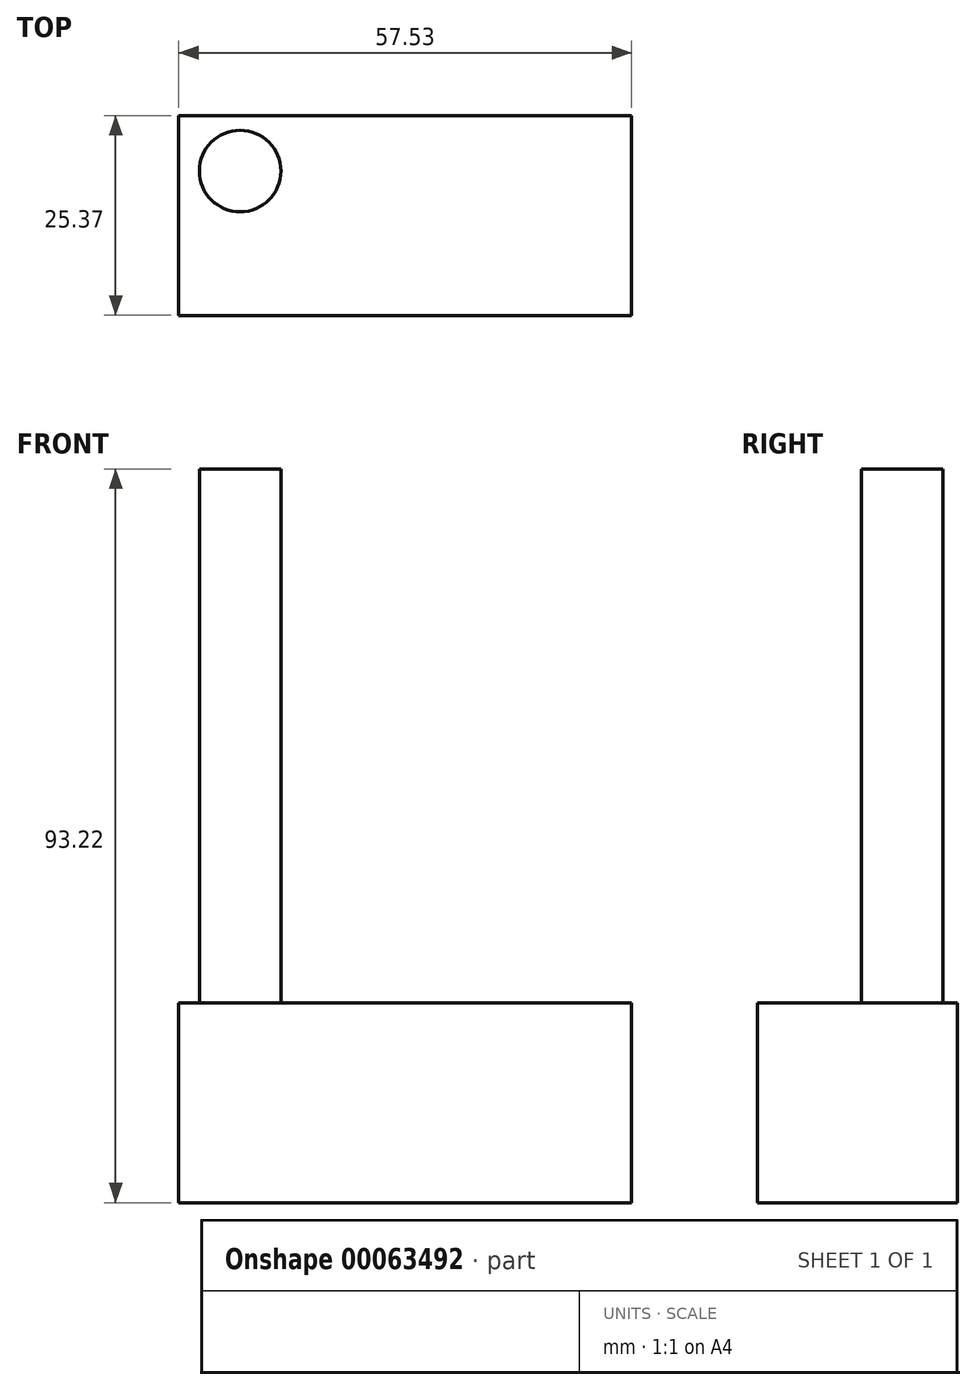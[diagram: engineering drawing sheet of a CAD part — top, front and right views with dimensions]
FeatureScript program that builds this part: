
annotation { "Feature Type Name" : "Feature", "Feature Type Description" : "" }
export const myFeature = defineFeature(function(context is Context, id is Id, definition is map)
    precondition{}
    {
        {
            var Q0;
            Q0=qCreatedBy(makeId("Top.planeOp"),FACE);
            var sketch = newSketch(context, id + "F0", { "sketchPlane" : qUnion([Q0])});
            skLineSegment(sketch, "E0.bottom", {"start": v(-28.89, 17.2) * mm, "end": v(28.64, 17.2) * mm});
            skLineSegment(sketch, "E0.top", {"start": v(-28.89, -8.16) * mm, "end": v(28.64, -8.16) * mm});
            skLineSegment(sketch, "E0.left", {"start": v(-28.89, 17.2) * mm, "end": v(-28.89, -8.16) * mm});
            skLineSegment(sketch, "E0.right", {"start": v(28.64, 17.2) * mm, "end": v(28.64, -8.16) * mm});
            skSolve(sketch);
        }
        {
            var Q0;
            Q0=makeQuery(id+"F0.imprint","IMPRINT",FACE,{"disambiguationData":[TD([[makeQuery(id+"F0.imprint","IMPRINT",EDGE,{"derivedFrom":sQuery(id+"F0.wireOp",EDGE,"E0.bottom")}),-1.0]])]});
            extrude(context, id + "F1", {"entities" : qUnion([Q0]), "depth" : 25.4 * mm});
        }
        {
            var Q0;
            Q0=makeQuery(id+"F1.opExtrude","CAP_FACE",FACE,{"disambiguationData":[OSD([sQuery(id+"F0.wireOp",EDGE,"E0.bottom"),sQuery(id+"F0.wireOp",EDGE,"E0.top"),sQuery(id+"F0.wireOp",EDGE,"E0.left"),sQuery(id+"F0.wireOp",EDGE,"E0.right")])],"isStart":false});
            var sketch = newSketch(context, id + "F2", { "sketchPlane" : qUnion([Q0])});
            skCircle(sketch, "E1", {"center": v(-21.1, 10.17) * mm, "radius": 5.18 * mm});
            skSolve(sketch);
        }
        {
            var Q0;
            Q0=makeQuery(id+"F2.imprint","IMPRINT",FACE,{"disambiguationData":[TD([[makeQuery(id+"F2.imprint","IMPRINT",EDGE,{"derivedFrom":sQuery(id+"F2.wireOp",EDGE,"E1")}),1.0]])]});
            extrude(context, id + "F3", {"entities" : qUnion([Q0]), "operationType" : NewBodyOperationType.ADD, "endBound" : BoundingType.THROUGH_ALL, "depth" : 25.4 * mm});
        }
    });
